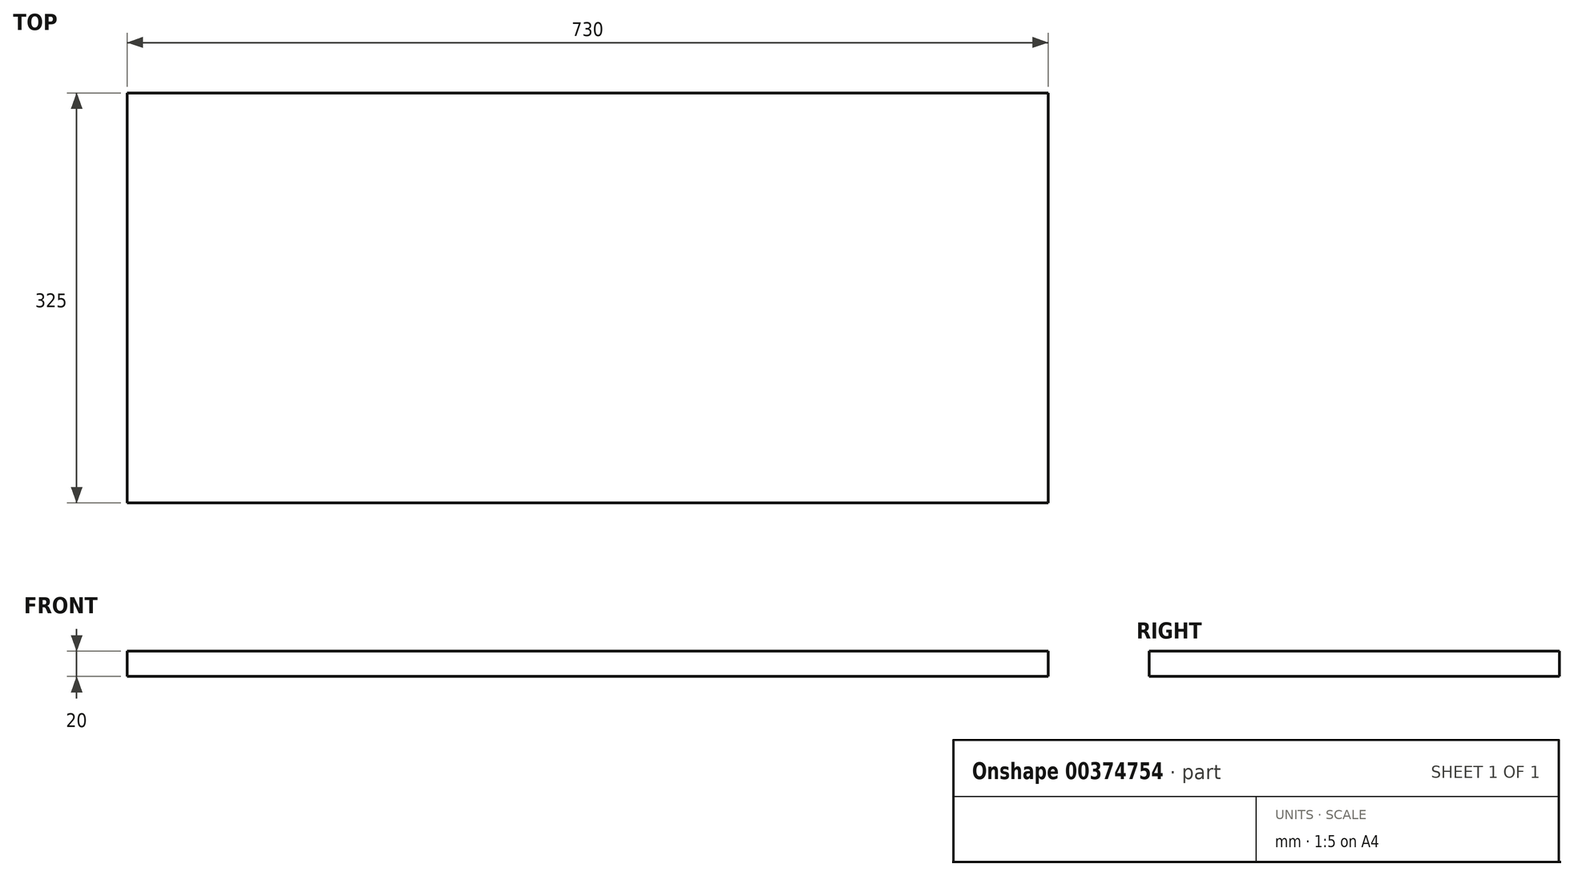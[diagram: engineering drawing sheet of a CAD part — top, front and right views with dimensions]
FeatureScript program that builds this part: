
annotation { "Feature Type Name" : "Feature", "Feature Type Description" : "" }
export const myFeature = defineFeature(function(context is Context, id is Id, definition is map)
    precondition{}
    {
        {
            var Q0;
            Q0=qCreatedBy(makeId("Top.planeOp"),FACE);
            var sketch = newSketch(context, id + "F0", { "sketchPlane" : qUnion([Q0])});
            skLineSegment(sketch, "E0.bottom", {"start": v(365, -162.5) * mm, "end": v(-365, -162.5) * mm});
            skLineSegment(sketch, "E0.top", {"start": v(365, 162.5) * mm, "end": v(-365, 162.5) * mm});
            skLineSegment(sketch, "E0.left", {"start": v(365, -162.5) * mm, "end": v(365, 162.5) * mm});
            skLineSegment(sketch, "E0.right", {"start": v(-365, -162.5) * mm, "end": v(-365, 162.5) * mm});
            skPoint(sketch, "E0.middle", {"position": v(0, 0) * mm});
            skSolve(sketch);
        }
        {
            var Q0;
            Q0=makeQuery(id+"F0.imprint","IMPRINT",FACE,{"disambiguationData":[TD([[makeQuery(id+"F0.imprint","IMPRINT",EDGE,{"derivedFrom":sQuery(id+"F0.wireOp",EDGE,"E0.bottom")}),-1.0]])]});
            extrude(context, id + "F1", {"entities" : qUnion([Q0]), "depth" : 20 * mm});
        }
    });
